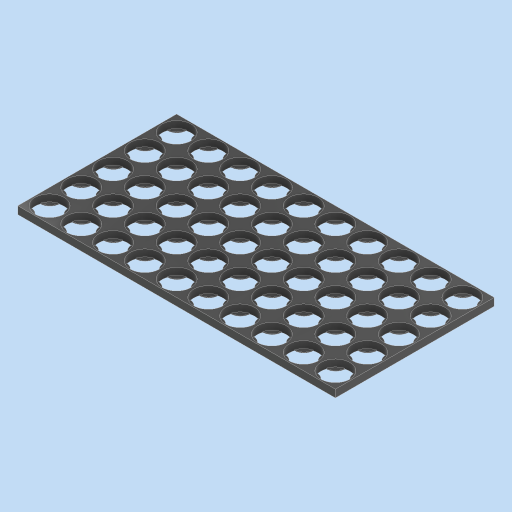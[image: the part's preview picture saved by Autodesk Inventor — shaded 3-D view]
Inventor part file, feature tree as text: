
AUTODESK INVENTOR PART (.ipt)
format: ipt  version: 2023 (Build 270158000, 158)  size: 512,512 bytes
history: native  units: in
note: dims shown in document units (in); Inventor stores cm internally (conversion verified against a paired STEP export)
features: extrude x2, other x1, sketch x1, pattern_linear x1
ambient origin geometry x8: Origin, YZ Plane, XZ Plane, XY Plane, X Axis, Y Axis, Z Axis, Center Point
bodies: Solid1 (feature_tree)
feature tree (5):
  parser-record x1  (decoder bookkeeping rows leaked as tree rows — omitted from the tree; the rows remain in map.json)
  sketch  "Sketch1"  dims[d0=0.8268in d1=0.9055in d2=0.1969in d3=0.0in d4=1.5748in d6=360.0deg d8=0.0197in d9=0.0in d10=3.937in d12=0.9055in d13=1.9685in d15=0.9055in]
  extrude  "Extrusion1"  Depth=0.9055in
  extrude  "Extrusion2"  Depth=0.1969in TaperAngle=0.0deg
  pattern_linear  "Rectangular Pattern1"  Count1=4 Spacing1=360.0deg
note: 1 file-system path scrubbed to <path> (originals preserved in map.json)
